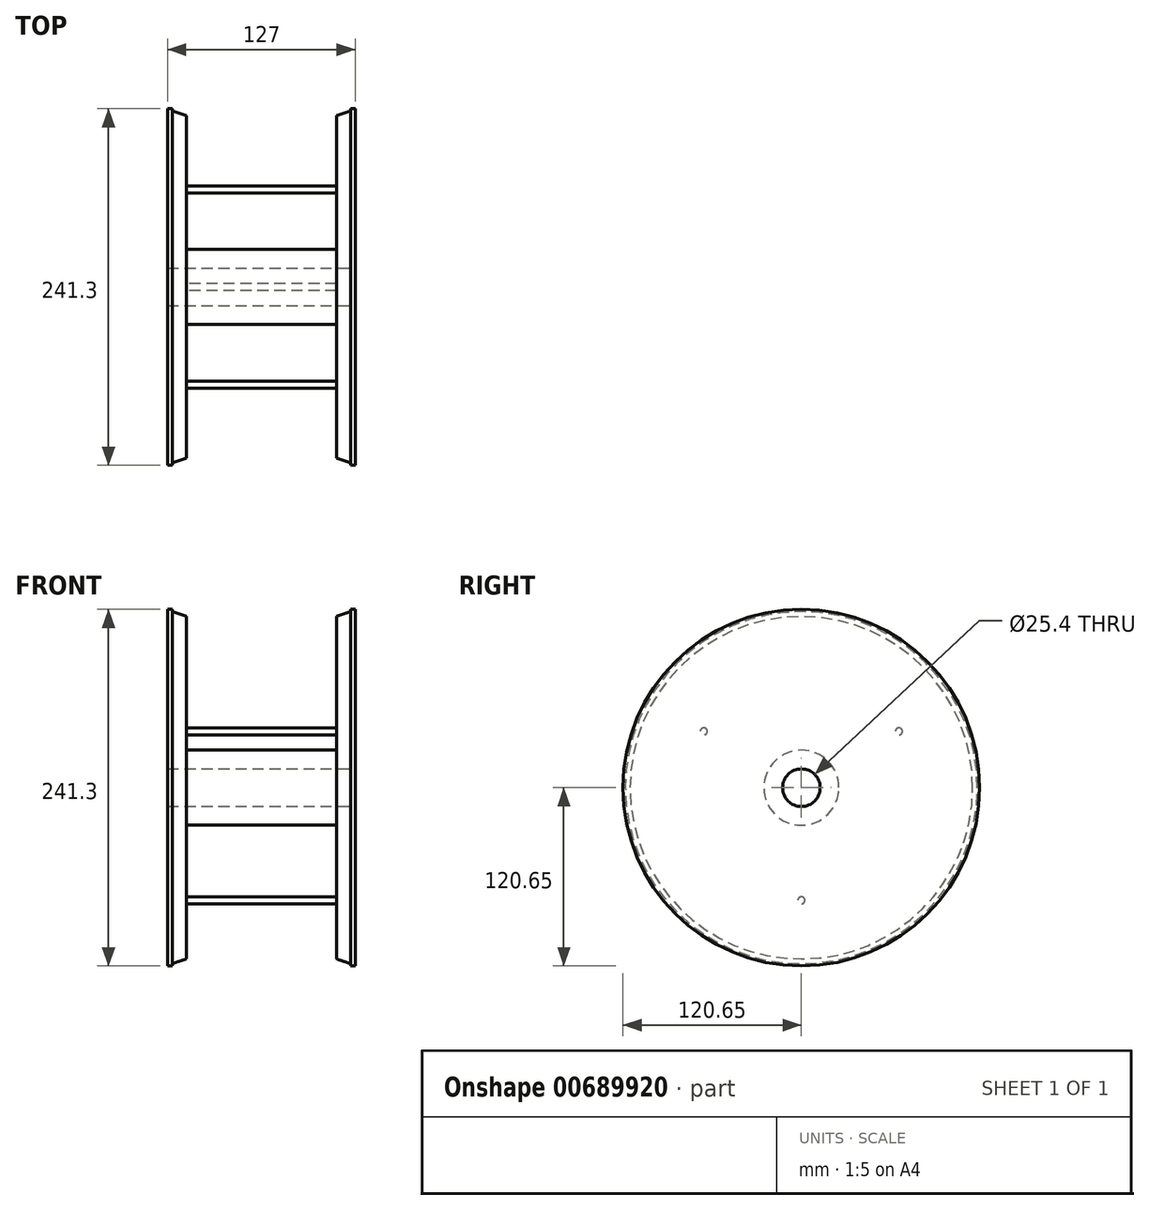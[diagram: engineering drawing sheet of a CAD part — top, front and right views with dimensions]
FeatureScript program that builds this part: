
annotation { "Feature Type Name" : "Feature", "Feature Type Description" : "" }
export const myFeature = defineFeature(function(context is Context, id is Id, definition is map)
    precondition{}
    {
        {
            var Q0;
            Q0=qCreatedBy(makeId("Right.planeOp"),FACE);
            var sketch = newSketch(context, id + "F0", { "sketchPlane" : qUnion([Q0])});
            skCircle(sketch, "E0", {"center": v(0, 0) * mm, "radius": 120.65 * mm});
            skSolve(sketch);
        }
        {
            var Q0;
            Q0=makeQuery(id+"F0.imprint","IMPRINT",FACE,{"disambiguationData":[TD([[makeQuery(id+"F0.imprint","IMPRINT",EDGE,{"derivedFrom":sQuery(id+"F0.wireOp",EDGE,"E0")}),1.0]])]});
            extrude(context, id + "F1", {"entities" : qUnion([Q0]), "depth" : 3.17 * mm, "offsetDistance" : 25.4 * mm});
        }
        {
            var Q0;
            Q0=makeQuery(id+"F1.opExtrude","CAP_FACE",FACE,{"disambiguationData":[OSD([sQuery(id+"F0.wireOp",EDGE,"E0")])],"isStart":false});
            var sketch = newSketch(context, id + "F2", { "sketchPlane" : qUnion([Q0])});
            skCircle(sketch, "E1", {"center": v(0, 0) * mm, "radius": 119.06 * mm});
            skSolve(sketch);
        }
        {
            var Q0;
            Q0 = qSketchRegion(id + "F2", true);
            extrude(context, id + "F3", {"entities" : qUnion([Q0]), "operationType" : NewBodyOperationType.ADD, "depth" : 9.52 * mm, "offsetDistance" : 25.4 * mm});
        }
        {
            var Q0;
            Q0=makeQuery(id+"F3.opExtrude","CAP_EDGE",EDGE,{"disambiguationData":[OSD([sQuery(id+"F2.wireOp",EDGE,"E1")])],"isStart":false});
            chamfer(context, id + "F4", {"entities" : qUnion([Q0]), "chamferType" : ChamferType.TWO_OFFSETS, "width1" : 3.17 * mm, "oppositeDirection" : false, "width2" : 9.52 * mm, "tangentPropagation" : true});
        }
        {
            var Q0;
            Q0=makeQuery(id+"F3.opExtrude","CAP_FACE",FACE,{"disambiguationData":[OSD([sQuery(id+"F2.wireOp",EDGE,"E1")])],"isStart":false});
            var sketch = newSketch(context, id + "F5", { "sketchPlane" : qUnion([Q0])});
            skCircle(sketch, "E2", {"center": v(0, 0) * mm, "radius": 25.4 * mm});
            skCircle(sketch, "E3", {"center": v(0, -76.2) * mm, "radius": 2.38 * mm});
            skLineSegment(sketch, "E4", {"start": v(0, 0) * mm, "end": v(21.15, 14.06) * mm});
            skLineSegment(sketch, "E5", {"start": v(0, -76.2) * mm, "end": v(0, 0) * mm, "construction": true});
            skPoint(sketch, "E6.end.orphan", {"position": v(-39.18, 22.74) * mm});
            skPoint(sketch, "E7.start.orphan", {"position": v(-78.36, 45.47) * mm});
            skCircle(sketch, "E8.1.0", {"center": v(66, 38.1) * mm, "radius": 2.38 * mm});
            skCircle(sketch, "E8.2.0", {"center": v(-66, 38.1) * mm, "radius": 2.38 * mm});
            skSolve(sketch);
        }
        {
            var Q0;
            Q0 = qSketchRegion(id + "F5", true);
            extrude(context, id + "F6", {"entities" : qUnion([Q0]), "operationType" : NewBodyOperationType.ADD, "depth" : 101.6 * mm, "offsetDistance" : 25.4 * mm});
        }
        {
            var Q0;
            Q0=makeQuery(id+"F6.opExtrude","CAP_FACE",FACE,{"disambiguationData":[OSD([sQuery(id+"F5.wireOp",EDGE,"E2")])],"isStart":false});
            var sketch = newSketch(context, id + "F7", { "sketchPlane" : qUnion([Q0])});
            skCircle(sketch, "E9", {"center": v(0, 0) * mm, "radius": 119.06 * mm});
            skSolve(sketch);
        }
        {
            var Q0;
            Q0 = qSketchRegion(id + "F7", true);
            extrude(context, id + "F8", {"entities" : qUnion([Q0]), "operationType" : NewBodyOperationType.ADD, "depth" : 9.52 * mm, "offsetDistance" : 25.4 * mm});
        }
        {
            var Q0;
            Q0=makeQuery(id+"F8.opExtrude","CAP_FACE",FACE,{"disambiguationData":[OSD([sQuery(id+"F7.wireOp",EDGE,"E9")])],"isStart":false});
            var sketch = newSketch(context, id + "F9", { "sketchPlane" : qUnion([Q0])});
            skCircle(sketch, "E10", {"center": v(0, 0) * mm, "radius": 120.65 * mm});
            skSolve(sketch);
        }
        {
            var Q0;
            Q0 = qSketchRegion(id + "F9", true);
            extrude(context, id + "F10", {"entities" : qUnion([Q0]), "operationType" : NewBodyOperationType.ADD, "depth" : 3.17 * mm, "offsetDistance" : 25.4 * mm});
        }
        {
            var Q0;
            Q0=makeQuery(id+"F8.opExtrude","CAP_EDGE",EDGE,{"disambiguationData":[OSD([sQuery(id+"F7.wireOp",EDGE,"E9")])],"isStart":true});
            chamfer(context, id + "F11", {"entities" : qUnion([Q0]), "chamferType" : ChamferType.TWO_OFFSETS, "width1" : 9.52 * mm, "oppositeDirection" : false, "width2" : 3.17 * mm, "tangentPropagation" : true});
        }
        {
            var Q0;
            Q0=makeQuery(id+"F10.opExtrude","CAP_FACE",FACE,{"disambiguationData":[OSD([sQuery(id+"F9.wireOp",EDGE,"E10")])],"isStart":false});
            var sketch = newSketch(context, id + "F12", { "sketchPlane" : qUnion([Q0])});
            skCircle(sketch, "E11", {"center": v(0, 0) * mm, "radius": 12.7 * mm});
            skSolve(sketch);
        }
        {
            var Q0;
            Q0 = qSketchRegion(id + "F12", true);
            extrude(context, id + "F13", {"entities" : qUnion([Q0]), "operationType" : NewBodyOperationType.REMOVE, "endBound" : BoundingType.THROUGH_ALL, "oppositeDirection" : true, "depth" : 25.4 * mm, "offsetDistance" : 25.4 * mm});
        }
    });
